# Revit family: Bike_Stall_CycleSafe-Angled-4-Bike
name_source: partatom
category: Site
revit_build: Autodesk Revit 2018 (Build: 20170927_1515(x64)
units: mm (PartAtom-declared; Revit-internal decimal feet)

## family parameters
Always vertical = Yes
Cut with Voids When Loaded = No
OmniClass Number = 23.40.10.11.11
OmniClass Title = Bicycle Racks
Part Type = Normal
Round Connector Dimension = Use Diameter
Shared = No
Work Plane-Based = No

## types (1)
- Bike_Stall_CycleSafe-Angled-4-Bike
    Fastener Material = Metal - Steel - CycleSafe - Powder Coat - Gray
    Height = 34 3/4"
    Keynote = 12 93 13
    Length = 79 3/4"
    Manufacturer = CycleSafe
    Rack Material = Metal - Steel - CycleSafe - Powder Coat - Gray
    Rail Signal Material = Plastic - PVC - CycleSafe - Red
    Rail Width = 1 81/128"
    Wheel Hanger Material = Metal - Steel - CycleSafe - Powder Coat
    Width = 28 77/256"

## geometry (parser evidence)
native form markers: Sweep x3
no freeform markers — native parametric forms only
